annotation { "Feature Type Name" : "Feature", "Feature Type Description" : "" }
export const myFeature = defineFeature(function(context is Context, id is Id, definition is map)
    precondition{}
    {
        {
            var Q0;
            Q0=qCreatedBy(makeId("Front.planeOp"),FACE);
            var sketch = newSketch(context, id + "F0", { "sketchPlane" : qUnion([Q0])});
            skLineSegment(sketch, "E0", {"start": v(-32.68, 80.3) * mm, "end": v(-32.68, -34) * mm});
            skLineSegment(sketch, "E1", {"start": v(-32.68, -34) * mm, "end": v(11.77, -34) * mm});
            skCircle(sketch, "E2", {"center": v(-32.68, 80.3) * mm, "radius": 9.53 * mm});
            skCircle(sketch, "E3", {"center": v(-32.68, 29.5) * mm, "radius": 15.88 * mm});
            skCircle(sketch, "E4", {"center": v(-32.68, -34) * mm, "radius": 10.08 * mm});
            skCircle(sketch, "E5", {"center": v(11.77, -34) * mm, "radius": 7.94 * mm});
            skLineSegment(sketch, "E6", {"start": v(-42.2, 80.65) * mm, "end": v(-48.43, 31.5) * mm});
            skLineSegment(sketch, "E7", {"start": v(-23.16, 80.33) * mm, "end": v(-16.93, 31.52) * mm});
            skLineSegment(sketch, "E8", {"start": v(-32.68, -44.07) * mm, "end": v(11.77, -41.93) * mm});
            skCircle(sketch, "E9", {"center": v(-32.68, 80.3) * mm, "radius": 3.18 * mm});
            skCircle(sketch, "E10", {"center": v(-32.68, 29.5) * mm, "radius": 3.18 * mm});
            skCircle(sketch, "E11", {"center": v(-32.68, -34) * mm, "radius": 3.18 * mm});
            skCircle(sketch, "E12", {"center": v(11.77, -34) * mm, "radius": 3.18 * mm});
            skPoint(sketch, "E13.newPointB", {"position": v(-22.6, -34) * mm});
            skArc(sketch, "E13.filletArc", {"start": v(-20.96, -16.17) * mm, "mid": v(-19.04, -22.1) * mm, "end": v(-13.42, -24.84) * mm});
            skCircle(sketch, "E14", {"center": v(-38.23, 66.03) * mm, "radius": 1.59 * mm});
            skPoint(sketch, "E15.end.orphan", {"position": v(-48.43, 27.41) * mm});
            skPoint(sketch, "E16.start.orphan", {"position": v(-16.93, 27.5) * mm});
            skLineSegment(sketch, "E17", {"start": v(-16.93, 27.5) * mm, "end": v(-22.6, -34) * mm});
            skLineSegment(sketch, "E18", {"start": v(-48.43, 31.5) * mm, "end": v(-42.72, -34.85) * mm});
            skPoint(sketch, "E19.end.orphan", {"position": v(11.77, -26.04) * mm});
            skLineSegment(sketch, "E20", {"start": v(-13.42, -24.84) * mm, "end": v(12.15, -26.06) * mm});
            skText(sketch, "E21", { "text": "JASMIN AMIR\n5.952", "fontName": "OpenSans-Italic.ttf"});
            const initialGuessF0  = {"E21": [0.01925, 0.00896, 1, 0, 0.02068]};
            skSetInitialGuess(sketch, initialGuessF0);
            skSolve(sketch);
        }
        {
            var Q0;
            Q0 = qSketchRegion(id + "F0", true);
            extrude(context, id + "F1", {"entities" : qUnion([Q0]), "depth" : 25.4 * mm, "offsetDistance" : 25.4 * mm});
        }
        {
            var Q0;
            Q0 = qSketchRegion(id + "F0", true);
            extrude(context, id + "F2", {"entities" : qUnion([Q0]), "operationType" : NewBodyOperationType.ADD, "depth" : 25.4 * mm, "offsetDistance" : 25.4 * mm});
        }
        {
            var Q0;
            Q0 = qSketchRegion(id + "F0", true);
            var Q1;
            {var subQ0=sQuery(id+"F0.wireOp",EDGE,"E4");var subQ1=sQuery(id+"F0.wireOp",EDGE,"E0");var subQ2=makeQuery(id+"F0.imprint","INTERSECT",VERTEX,{"derivedFrom":[subQ1,subQ0]});Q1=makeQuery(id+"F0.imprint","IMPRINT",FACE,{"disambiguationData":[TD([[makeQuery(id+"F0.imprint","IMPRINT",EDGE,{"disambiguationData":[TD([[subQ2,-1.0]])],"derivedFrom":subQ1}),1.0]])]});}
            extrude(context, id + "F3", {"entities" : qUnion([Q0, Q1]), "operationType" : NewBodyOperationType.ADD, "depth" : 25.4 * mm, "offsetDistance" : 25.4 * mm});
        }
    });